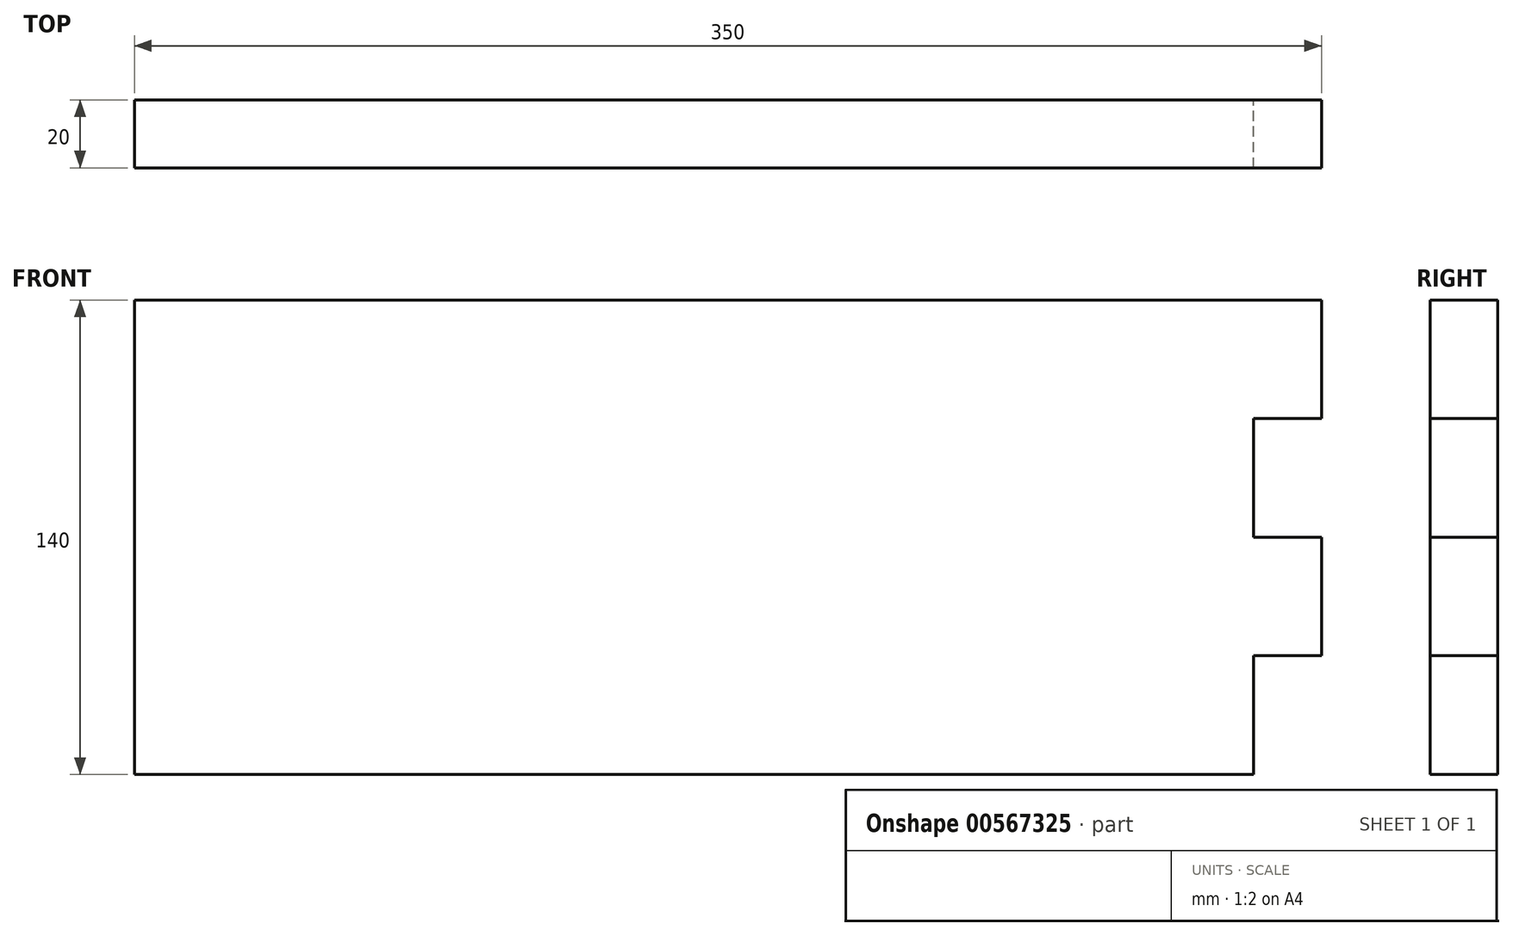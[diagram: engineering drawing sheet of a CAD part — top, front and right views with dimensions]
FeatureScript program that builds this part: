
annotation { "Feature Type Name" : "Feature", "Feature Type Description" : "" }
export const myFeature = defineFeature(function(context is Context, id is Id, definition is map)
    precondition{}
    {
        {
            var Q0;
            Q0=qCreatedBy(makeId("Front.planeOp"),FACE);
            var sketch = newSketch(context, id + "F0", { "sketchPlane" : qUnion([Q0])});
            skLineSegment(sketch, "E0.bottom", {"start": v(0, 0) * mm, "end": v(330, 0) * mm});
            skLineSegment(sketch, "E0.top", {"start": v(0, 140) * mm, "end": v(350, 140) * mm});
            skLineSegment(sketch, "E0.left", {"start": v(0, 0) * mm, "end": v(0, 140) * mm});
            skLineSegment(sketch, "E0.right", {"start": v(350, 35) * mm, "end": v(350, 70) * mm});
            skLineSegment(sketch, "E1", {"start": v(330, 105) * mm, "end": v(330, 70) * mm});
            skLineSegment(sketch, "E2", {"start": v(330, 70) * mm, "end": v(350, 70) * mm});
            skLineSegment(sketch, "E3.0", {"start": v(330, 105) * mm, "end": v(350, 105) * mm});
            skLineSegment(sketch, "E4.0", {"start": v(330, 35) * mm, "end": v(350, 35) * mm});
            skPoint(sketch, "E5.orphan", {"position": v(330, 140) * mm});
            skLineSegment(sketch, "E6.trimOffspring", {"start": v(350, 105) * mm, "end": v(350, 140) * mm});
            skLineSegment(sketch, "E7.trimOffspring", {"start": v(330, 35) * mm, "end": v(330, 0) * mm});
            skPoint(sketch, "E8.orphan", {"position": v(350, 0) * mm});
            skSolve(sketch);
        }
        {
            var Q0;
            Q0=makeQuery(id+"F0.imprint","IMPRINT",FACE,{"disambiguationData":[TD([[makeQuery(id+"F0.imprint","IMPRINT",EDGE,{"derivedFrom":sQuery(id+"F0.wireOp",EDGE,"E0.bottom")}),1.0]])]});
            extrude(context, id + "F1", {"entities" : qUnion([Q0]), "depth" : 20 * mm, "offsetDistance" : 25 * mm});
        }
    });
